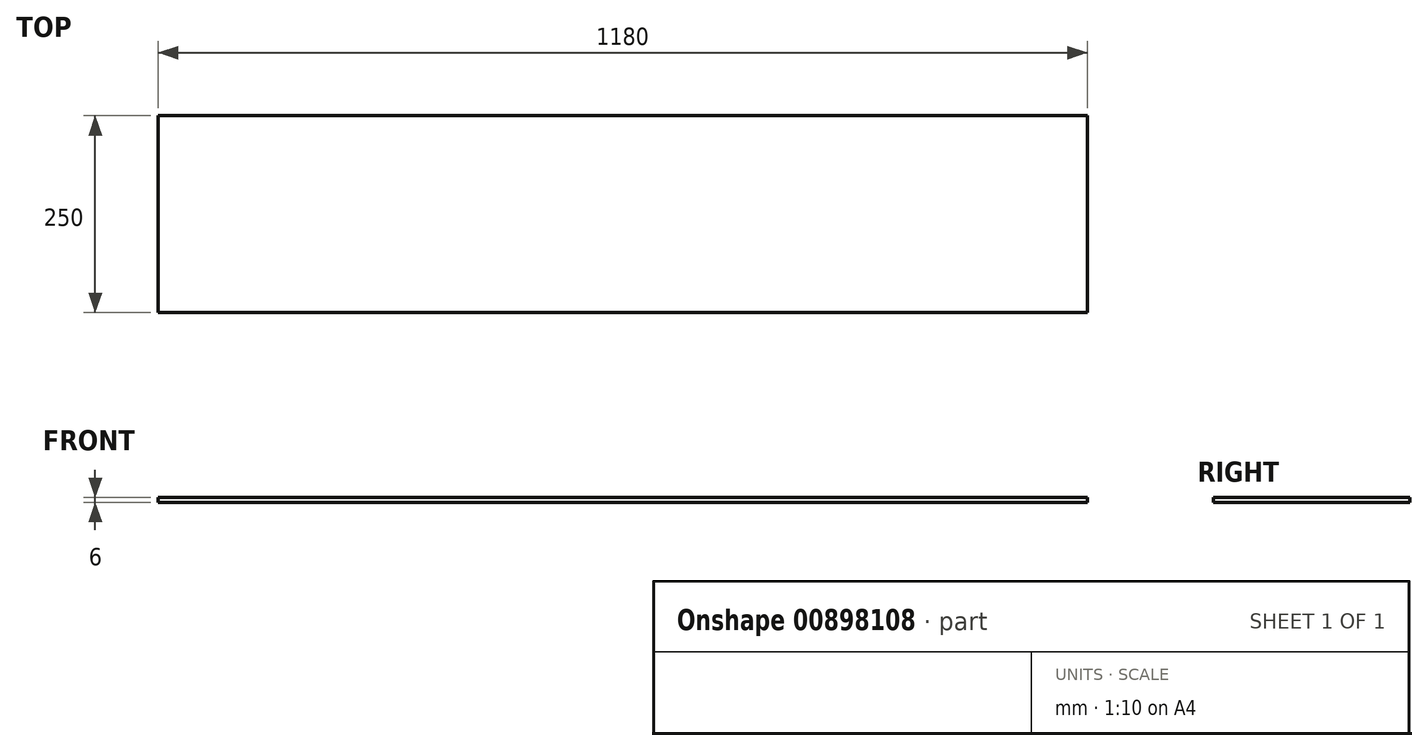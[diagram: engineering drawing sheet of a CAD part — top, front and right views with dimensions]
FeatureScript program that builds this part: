
annotation { "Feature Type Name" : "Feature", "Feature Type Description" : "" }
export const myFeature = defineFeature(function(context is Context, id is Id, definition is map)
    precondition{}
    {
        {
            var Q0;
            Q0=qCreatedBy(makeId("Front.planeOp"),FACE);
            var sketch = newSketch(context, id + "F0", { "sketchPlane" : qUnion([Q0])});
            skLineSegment(sketch, "E0.bottom", {"start": v(0, 0) * mm, "end": v(1180, 0) * mm});
            skLineSegment(sketch, "E0.top", {"start": v(0, 6) * mm, "end": v(1180, 6) * mm});
            skLineSegment(sketch, "E0.left", {"start": v(0, 0) * mm, "end": v(0, 6) * mm});
            skLineSegment(sketch, "E0.right", {"start": v(1180, 0) * mm, "end": v(1180, 6) * mm});
            skSolve(sketch);
        }
        {
            var Q0;
            Q0=qSketchRegion(id+"F0",true);
            extrude(context, id + "F1", {"entities" : qUnion([Q0]), "depth" : 250 * mm, "offsetDistance" : 25 * mm});
        }
    });
